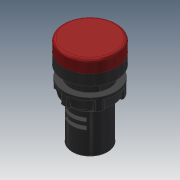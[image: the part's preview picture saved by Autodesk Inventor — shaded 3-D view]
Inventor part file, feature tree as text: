
AUTODESK INVENTOR PART (.ipt)
format: ipt  version: 2020.3 (Build 243373000, 373)  size: 320,000 bytes
history: native  units: in
note: dims shown in document units (in); Inventor stores cm internally (conversion verified against a paired STEP export)
features: fillet x3, other x1, pattern_circular x1, mirror x1
ambient origin geometry x8: Origin, YZ Plane, XZ Plane, XY Plane, X Axis, Y Axis, Z Axis, Center Point
bodies: Solid1 (feature_tree), Solid2 (feature_tree), Solid3 (feature_tree), Solid4 (feature_tree), Solid5 (feature_tree), Solid6 (feature_tree)
feature tree (6):
  fillet  "Fillet1"  [1 undecoded]
  other  "Boss-Extrude5"
  pattern_circular  "CirPattern1"
  fillet  "Fillet5"  [1 undecoded]
  fillet  "Fillet4"  [1 undecoded]
  mirror  "Mirror1"
note: 3 required parameter values undecoded (feature->parameter linkage not recoverable at this tier; creation-order binding heuristic only, values carry confidence <= 0.55)
